# Revit family: Gira_0214411
name_source: partatom
category: Elektroinstallationen
revit_build: Autodesk Revit 2017 (Build: 20160225_1515(x64)
units: mm (PartAtom-declared; Revit-internal decimal feet)

## family parameters
Basisbauteil = Fläche
Beim Laden mit Abzugskörper schneiden = Nein
Bemaßung runder Anschluss = Durchmesser verwenden
Beschriftungsausrichtung beibehalten = Nein
Gemeinsam genutzt = Nein
Raumberechnungspunkt = Nein
Teiletyp = Normal

## types (1)
- Abdeckrahmen 4f Gira E3 Hellgrau/Reinweiß
    Anzahl der Einheiten = 4
    Anzahl der Einheiten horizontal = 4
    Anzahl der Einheiten vertikal = 4
    Bauelement = E3_Rahmen_4fach
    Befestigungsart = Klemmbefestigung
    Beschreibung = Abdeckrahmen Gira E3 Hellgrau Soft-Touch mit Trägerrahmen Reinweiß glänzend 4fach Merkmale: - Bruchsicher.  Hinweise : - Soft-Touch-Oberfläche. - NCS-Wert: ähnl. NCS S-2000 N
    Farbe = grau
    GTIN = 4010337023807
    Geeignet für Einbauinstallation = Nein
    Geeignet für Geräteeinbaukanal = Nein
    Geeignet für Unterflurkanaldose = Nein
    Geeignet für Unterputz-Installation = Ja
    HAN = 0214411
    Halogenfrei = Nein
    HeinzeBIM = https://bimportal.heinze.de
    Hersteller = Gira
    Kategorie = Abdeckrahmen
    Mit Klappdeckel = Nein
    Mit Montagerahmen = Nein
    Montagerichtung = horizontal und vertikal
    Name = Abdeckrahmen 4f Gira E3 Hellgrau/Reinweiß
    Oberfläche = sonstige
    Region = DE
    Schutzart (IP) = IP20
    Textfeld/Beschriftungsfläche = Nein
    Transparent = Nein
    URL = http://katalog.gira.de
    Verfügbar = Ja
    Vorgabe-Ansicht = 1219 mm
    Werkstoff = sonstige
    Werkstoffgüte = sonstige

## geometry (parser evidence)
native form markers: Sweep x2
no freeform markers — native parametric forms only
